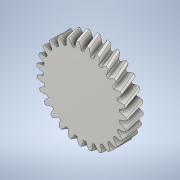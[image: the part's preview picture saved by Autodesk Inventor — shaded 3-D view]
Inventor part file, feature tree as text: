
AUTODESK INVENTOR PART (.ipt)
format: ipt  version: 2020 (Build 240168000, 168)  size: 503,808 bytes
history: native  units: mm (DEFAULTED — no unit token found)
features: plane x3, other x3, sketch x2, extrude x1
ambient origin geometry x8: Origin, YZ Plane, XZ Plane, XY Plane, X Axis, Y Axis, Z Axis, Center Point
bodies: Solid1 (feature_tree)
feature tree (9):
  extrude  "Extrusion1"  Depth=5.0mm TaperAngle=0.0deg
  plane  "Work Plane2"
  plane  "Work Plane8"
  plane  "Work Plane9"
  other  "Spur Gear"
  sketch  "Sketch1"  dims[d0=26.262248mm d1=5.0mm d2=0.0mm]
  sketch  "Sketch2"  dims[d3=24.545455mm d4=10.0mm d5=0.0mm d16=25.0mm d17=0.0mm d34=1.163553mm d39=0.0mm d41=0.0mm d43=25.0mm d46=25.0mm d47=0.0mm d48=0.0mm]
  other  "Srf1"
  other  "Pitch Diameter"
